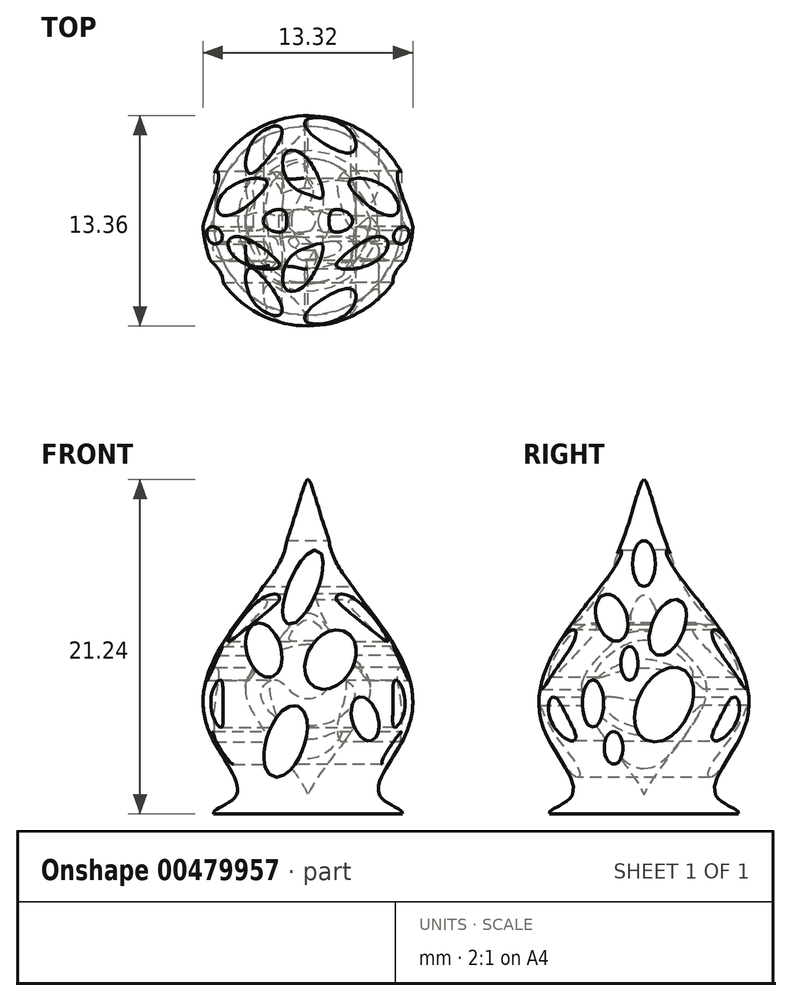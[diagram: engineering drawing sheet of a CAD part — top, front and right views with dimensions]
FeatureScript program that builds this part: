
annotation { "Feature Type Name" : "Feature", "Feature Type Description" : "" }
export const myFeature = defineFeature(function(context is Context, id is Id, definition is map)
    precondition{}
    {
        {
            var Q0;
            Q0=qCreatedBy(makeId("Front.planeOp"),FACE);
            var sketch = newSketch(context, id + "F0", { "sketchPlane" : qUnion([Q0])});
            skLineSegment(sketch, "E0", {"start": v(-12.63, -18.43) * mm, "end": v(-6.63, -18.43) * mm});
            skFitSpline(sketch, "E1", {"points": [v(-12.63, -18.43) * mm, v(-11.19, -17.25) * mm, v(-13.15, -12.56) * mm, v(-11.35, -6.54) * mm, v(-8.24, -1.74) * mm, v(-6.63, 2.81) * mm, v(-6.63, -1.89) * mm, v(-8.5, -7.42) * mm, v(-10.53, -11.13) * mm, v(-6.63, -18.43) * mm, v(-12.63, -18.43) * mm]});
            skLineSegment(sketch, "E2", {"start": v(-6.63, -18.43) * mm, "end": v(-6.63, 2.81) * mm});
            skSolve(sketch);
        }
        {
            var Q0;
            {var subQ4=sQuery(id+"F0.wireOp",EDGE,"E0");Q0=makeQuery(id+"F0.imprint","IMPRINT",FACE,{"disambiguationData":[TD([[makeQuery(id+"F0.imprint","IMPRINT",EDGE,{"derivedFrom":subQ4}),1.0]])]});}
            var Q1;
            Q1=sQuery(id+"F0.wireOp",EDGE,"E2");
            revolve(context, id + "F1", {"entities" : qUnion([Q0]), "axis" : qUnion([Q1]), "revolveType" : RevolveType.FULL});
        }
        {
            var Q0;
            Q0=qCreatedBy(makeId("Front.planeOp"),FACE);
            var sketch = newSketch(context, id + "F2", { "sketchPlane" : qUnion([Q0])});
            skEllipse(sketch, "E3", {"center": v(-6.95, -4.03) * mm, "majorRadius": 2.53 * mm, "minorRadius": 0.92 * mm, "majorAxis": v(-0.38, -0.92)});
            skEllipse(sketch, "E4", {"center": v(-9.43, -8.03) * mm, "majorRadius": 1.77 * mm, "minorRadius": 1.08 * mm, "majorAxis": v(0.28, -0.96)});
            skEllipse(sketch, "E5", {"center": v(-5.2, -8.63) * mm, "majorRadius": 2.02 * mm, "minorRadius": 1.48 * mm, "majorAxis": v(-0.5, -0.87)});
            skEllipse(sketch, "E6", {"center": v(-8.05, -13.82) * mm, "majorRadius": 2.38 * mm, "minorRadius": 1.21 * mm, "majorAxis": v(0.33, 0.94)});
            skEllipse(sketch, "E7", {"center": v(-3, -12.4) * mm, "majorRadius": 1.44 * mm, "minorRadius": 0.82 * mm, "majorAxis": v(0.29, -0.96)});
            skSolve(sketch);
        }
        {
            var Q0;
            Q0 = qSketchRegion(id + "F2", true);
            extrude(context, id + "F3", {"entities" : qUnion([Q0]), "operationType" : NewBodyOperationType.REMOVE, "endBound" : BoundingType.SYMMETRIC, "oppositeDirection" : true, "depth" : 25 * mm});
        }
        {
            var Q0;
            Q0=qCreatedBy(makeId("Right.planeOp"),FACE);
            var sketch = newSketch(context, id + "F4", { "sketchPlane" : qUnion([Q0])});
            skEllipse(sketch, "E8", {"center": v(-2.04, -5.97) * mm, "majorRadius": 1.55 * mm, "minorRadius": 0.96 * mm, "majorAxis": v(0.32, -0.95)});
            skEllipse(sketch, "E9", {"center": v(1.51, -6.59) * mm, "majorRadius": 1.89 * mm, "minorRadius": 1.02 * mm, "majorAxis": v(-0.39, -0.92)});
            skEllipse(sketch, "E10", {"center": v(-0.92, -8.87) * mm, "majorRadius": 1.08 * mm, "minorRadius": 0.54 * mm, "majorAxis": v(0, -1)});
            skEllipse(sketch, "E11", {"center": v(-3.24, -11.42) * mm, "majorRadius": 1.5 * mm, "minorRadius": 0.68 * mm, "majorAxis": v(0, 1)});
            skEllipse(sketch, "E12", {"center": v(1.28, -11.5) * mm, "majorRadius": 1.66 * mm, "minorRadius": 2.54 * mm, "majorAxis": v(-0.88, 0.47)});
            skEllipse(sketch, "E13", {"center": v(0, -2.53) * mm, "majorRadius": 1.47 * mm, "minorRadius": 0.72 * mm, "majorAxis": v(0, -1)});
            skEllipse(sketch, "E14", {"center": v(-1.92, -14.24) * mm, "majorRadius": 1.04 * mm, "minorRadius": 0.6 * mm, "majorAxis": v(0, 1)});
            skSolve(sketch);
        }
        {
            var Q0;
            Q0 = qSketchRegion(id + "F4", true);
            extrude(context, id + "F5", {"entities" : qUnion([Q0]), "operationType" : NewBodyOperationType.REMOVE, "endBound" : BoundingType.SYMMETRIC, "oppositeDirection" : true, "depth" : 32.2 * mm});
        }
    });
